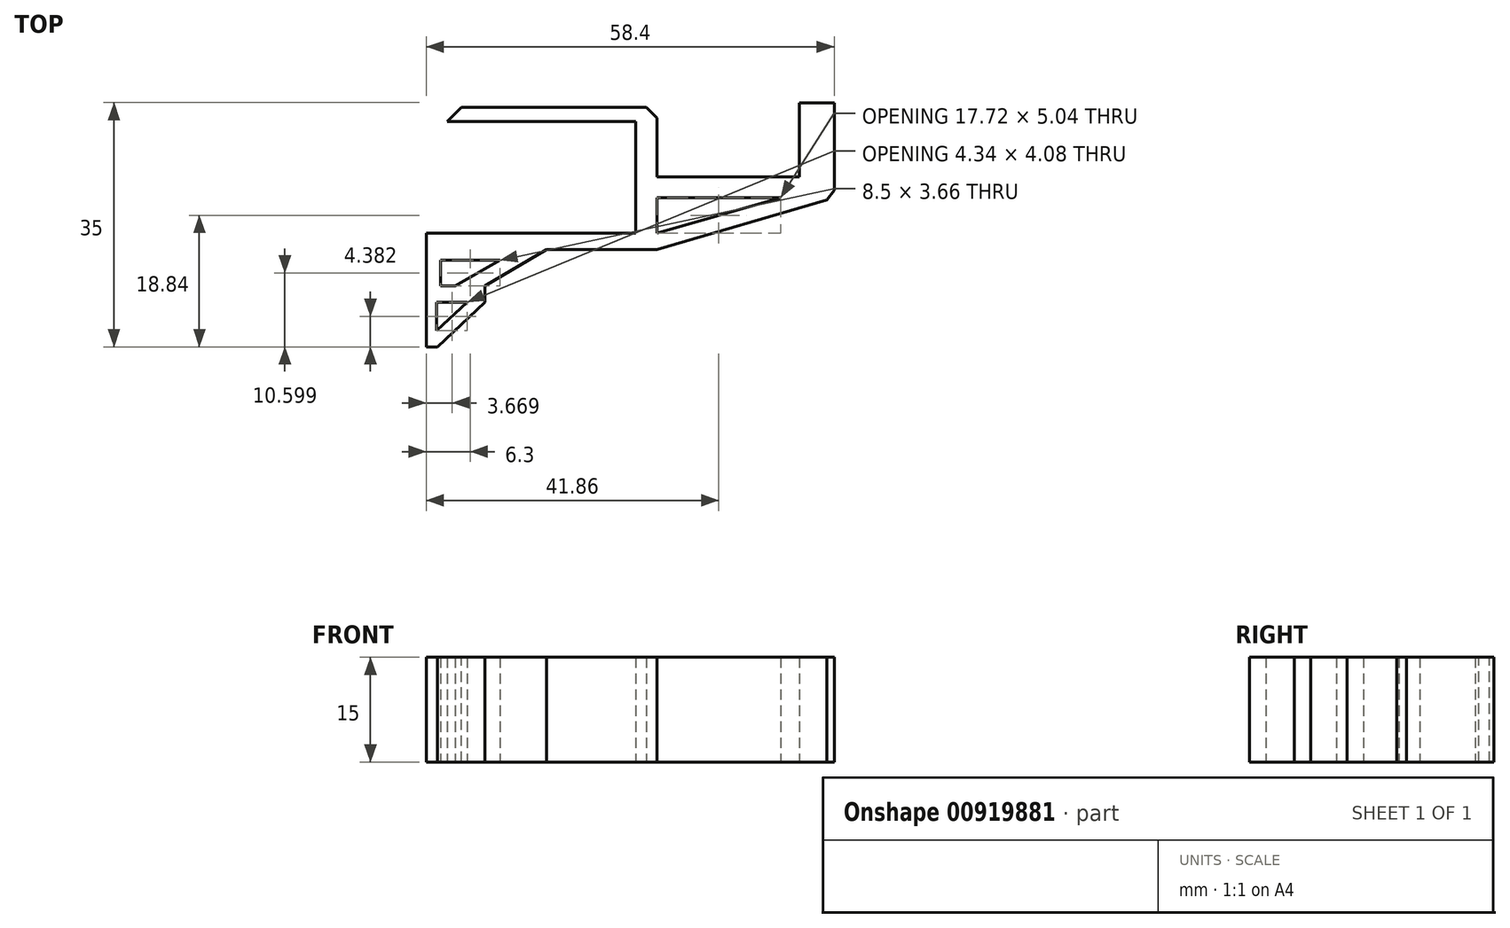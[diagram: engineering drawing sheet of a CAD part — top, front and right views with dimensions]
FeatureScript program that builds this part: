
annotation { "Feature Type Name" : "Feature", "Feature Type Description" : "" }
export const myFeature = defineFeature(function(context is Context, id is Id, definition is map)
    precondition{}
    {
        {
            var Q0;
            Q0=qCreatedBy(makeId("Top.planeOp"),FACE);
            var sketch = newSketch(context, id + "F0", { "sketchPlane" : qUnion([Q0])});
            skLineSegment(sketch, "E0", {"start": v(0, 0) * mm, "end": v(0, 16) * mm});
            skLineSegment(sketch, "E1", {"start": v(0, 16) * mm, "end": v(-27, 16) * mm});
            skLineSegment(sketch, "E2", {"start": v(-27, 16) * mm, "end": v(-27, 18) * mm});
            skLineSegment(sketch, "E3", {"start": v(-27, 18) * mm, "end": v(3, 18) * mm});
            skLineSegment(sketch, "E4", {"start": v(0, 0) * mm, "end": v(-30, 0) * mm});
            skLineSegment(sketch, "E5", {"start": v(-30, 0) * mm, "end": v(-30, -2.38) * mm});
            skLineSegment(sketch, "E6", {"start": v(-30, -2.38) * mm, "end": v(-30, -16.32) * mm});
            skLineSegment(sketch, "E7", {"start": v(-30, -16.32) * mm, "end": v(-28.43, -16.32) * mm});
            skLineSegment(sketch, "E8", {"start": v(-28.43, -16.32) * mm, "end": v(-21.6, -9.9) * mm});
            skLineSegment(sketch, "E9", {"start": v(-21.6, -9.9) * mm, "end": v(-21.6, -7.55) * mm});
            skLineSegment(sketch, "E10", {"start": v(-21.6, -7.55) * mm, "end": v(-12.75, -2.38) * mm});
            skLineSegment(sketch, "E11", {"start": v(-19.45, -3.9) * mm, "end": v(-25.88, -7.55) * mm});
            skLineSegment(sketch, "E12", {"start": v(-25.88, -7.55) * mm, "end": v(-27.95, -7.55) * mm});
            skLineSegment(sketch, "E13", {"start": v(-27.95, -7.55) * mm, "end": v(-27.95, -3.9) * mm});
            skLineSegment(sketch, "E14", {"start": v(-27.95, -3.9) * mm, "end": v(-19.45, -3.9) * mm});
            skLineSegment(sketch, "E15", {"start": v(-28.5, -10.73) * mm, "end": v(-28.5, -13.98) * mm});
            skLineSegment(sketch, "E16", {"start": v(-28.5, -13.98) * mm, "end": v(-24.16, -9.9) * mm});
            skLineSegment(sketch, "E17", {"start": v(-24.16, -9.9) * mm, "end": v(-28.5, -9.9) * mm});
            skLineSegment(sketch, "E18", {"start": v(-28.5, -9.9) * mm, "end": v(-28.5, -10.73) * mm});
            skLineSegment(sketch, "E19", {"start": v(-12.75, -2.38) * mm, "end": v(3, -2.38) * mm});
            skLineSegment(sketch, "E20", {"start": v(3, 8.04) * mm, "end": v(23.4, 8.04) * mm});
            skLineSegment(sketch, "E21", {"start": v(23.4, 8.04) * mm, "end": v(23.4, 18.68) * mm});
            skLineSegment(sketch, "E22", {"start": v(23.4, 18.68) * mm, "end": v(28.4, 18.68) * mm});
            skLineSegment(sketch, "E23", {"start": v(28.4, 18.68) * mm, "end": v(28.4, 5.04) * mm});
            skLineSegment(sketch, "E24", {"start": v(28.4, 5.04) * mm, "end": v(3, 5.04) * mm});
            skLineSegment(sketch, "E25", {"start": v(3, -2.38) * mm, "end": v(28.4, 5.04) * mm});
            skLineSegment(sketch, "E26", {"start": v(3, 0) * mm, "end": v(20.72, 5.04) * mm});
            skLineSegment(sketch, "E27", {"start": v(3, 18) * mm, "end": v(3, 8.04) * mm});
            skLineSegment(sketch, "E28", {"start": v(3, 0) * mm, "end": v(3, 5.04) * mm});
            skSolve(sketch);
        }
        {
            var Q0;
            Q0=makeQuery(id+"F0.imprint","IMPRINT",FACE,{"disambiguationData":[TD([[makeQuery(id+"F0.imprint","IMPRINT",EDGE,{"derivedFrom":sQuery(id+"F0.wireOp",EDGE,"E0")}),-1.0]])]});
            extrude(context, id + "F1", {"entities" : qUnion([Q0]), "depth" : 15 * mm, "offsetDistance" : 25.4 * mm});
        }
        {
            var Q0;
            Q0=makeQuery(id+"F1.opExtrude","SWEPT_EDGE",EDGE,{"disambiguationData":[OSD([sQuery(id+"F0.wireOp",EDGE,"E3"),sQuery(id+"F0.wireOp",EDGE,"E27")])]});
            var Q1;
            Q1=makeQuery(id+"F1.opExtrude","SWEPT_EDGE",EDGE,{"disambiguationData":[OSD([sQuery(id+"F0.wireOp",EDGE,"E23"),sQuery(id+"F0.wireOp",EDGE,"E25")])]});
            chamfer(context, id + "F2", {"entities" : qUnion([Q0, Q1]), "width" : 1.5 * mm, "tangentPropagation" : true});
        }
        {
            var Q0;
            Q0=makeQuery(id+"F1.opExtrude","SWEPT_EDGE",EDGE,{"disambiguationData":[OSD([sQuery(id+"F0.wireOp",EDGE,"E2"),sQuery(id+"F0.wireOp",EDGE,"E3")])]});
            chamfer(context, id + "F3", {"entities" : qUnion([Q0]), "width" : 2 * mm, "tangentPropagation" : true});
        }
    });
